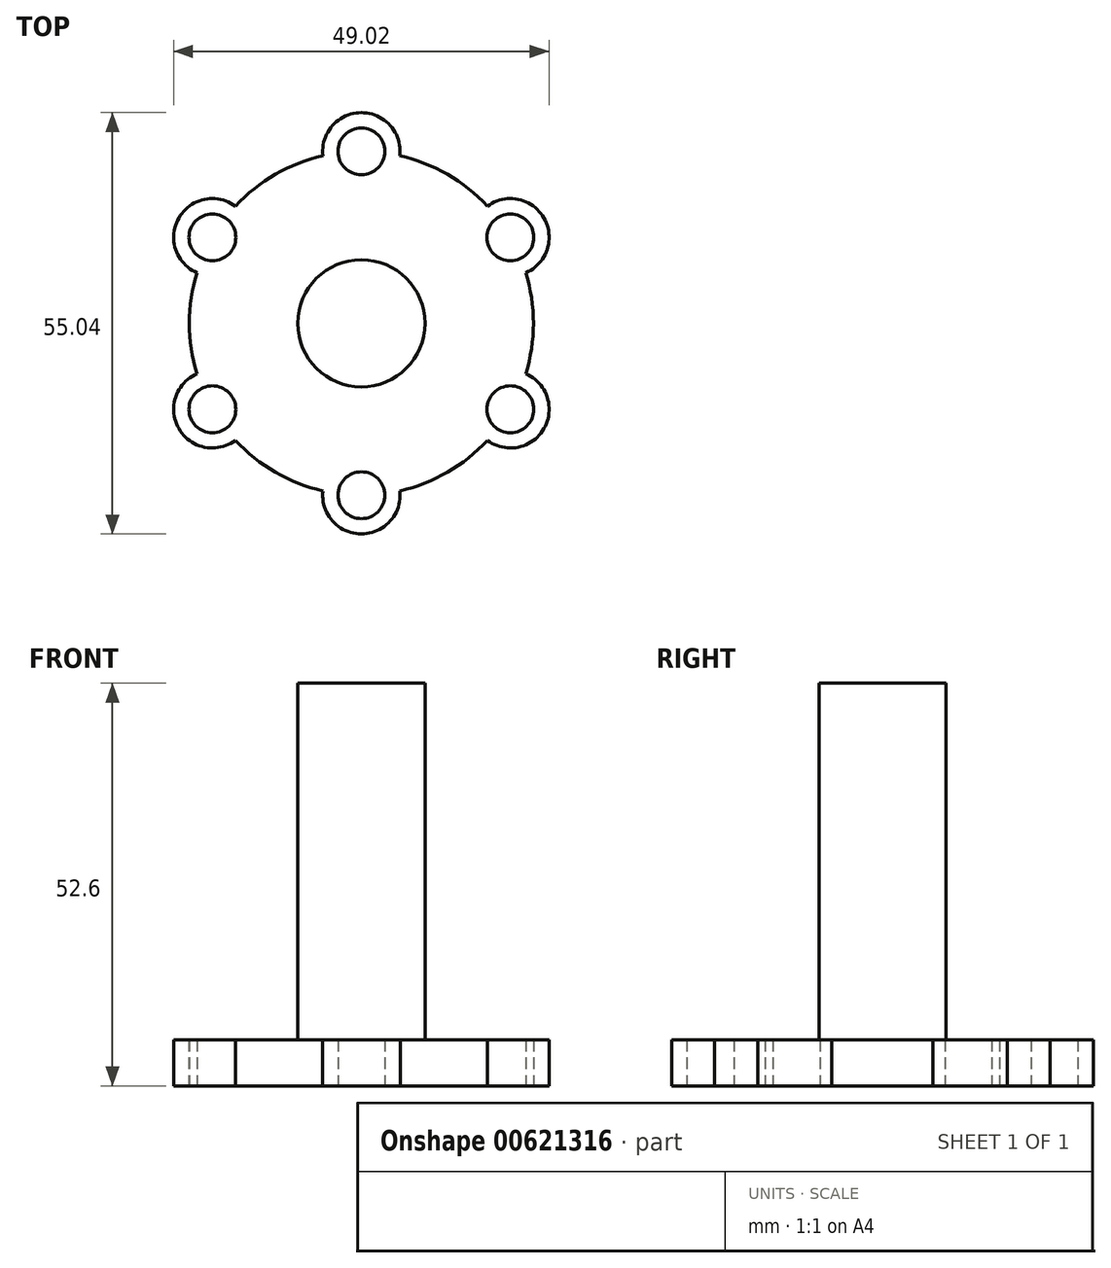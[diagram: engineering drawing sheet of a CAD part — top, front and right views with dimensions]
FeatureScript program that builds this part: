
annotation { "Feature Type Name" : "Feature", "Feature Type Description" : "" }
export const myFeature = defineFeature(function(context is Context, id is Id, definition is map)
    precondition{}
    {
        {
            var Q0;
            Q0=qCreatedBy(makeId("Top.planeOp"),FACE);
            var sketch = newSketch(context, id + "F0", { "sketchPlane" : qUnion([Q0])});
            skCircle(sketch, "E0", {"center": v(0, 0) * mm, "radius": 22.46 * mm});
            skCircle(sketch, "E1", {"center": v(0, 0) * mm, "radius": 8.3 * mm});
            skArc(sketch, "E2", {"start": v(3.05, 22.25) * mm, "mid": v(0, 25.52) * mm, "end": v(-3.05, 22.25) * mm});
            skCircle(sketch, "E3.0", {"center": v(0, 0) * mm, "radius": 20.46 * mm});
            skArc(sketch, "E4.0", {"start": v(5.03, 21.9) * mm, "mid": v(0, 27.52) * mm, "end": v(-5.03, 21.9) * mm});
            skArc(sketch, "E5.1.0", {"start": v(-16.45, 15.3) * mm, "mid": v(-23.83, 13.76) * mm, "end": v(-21.47, 6.6) * mm});
            skArc(sketch, "E5.1.1", {"start": v(-17.75, 13.77) * mm, "mid": v(-22.1, 12.76) * mm, "end": v(-20.8, 8.48) * mm});
            skArc(sketch, "E5.2.0", {"start": v(-21.47, -6.6) * mm, "mid": v(-23.83, -13.76) * mm, "end": v(-16.45, -15.3) * mm});
            skArc(sketch, "E5.2.1", {"start": v(-20.8, -8.48) * mm, "mid": v(-22.1, -12.76) * mm, "end": v(-17.75, -13.77) * mm});
            skArc(sketch, "E5.3.0", {"start": v(-5.03, -21.9) * mm, "mid": v(0, -27.52) * mm, "end": v(5.03, -21.9) * mm});
            skArc(sketch, "E5.3.1", {"start": v(-3.05, -22.25) * mm, "mid": v(0, -25.52) * mm, "end": v(3.05, -22.25) * mm});
            skArc(sketch, "E5.4.0", {"start": v(16.45, -15.3) * mm, "mid": v(23.83, -13.76) * mm, "end": v(21.47, -6.6) * mm});
            skArc(sketch, "E5.4.1", {"start": v(17.75, -13.77) * mm, "mid": v(22.1, -12.76) * mm, "end": v(20.8, -8.48) * mm});
            skArc(sketch, "E5.5.0", {"start": v(21.47, 6.6) * mm, "mid": v(23.83, 13.76) * mm, "end": v(16.45, 15.3) * mm});
            skArc(sketch, "E5.5.1", {"start": v(20.8, 8.48) * mm, "mid": v(22.1, 12.76) * mm, "end": v(17.75, 13.77) * mm});
            skCircle(sketch, "E6", {"center": v(-19.45, -11.23) * mm, "radius": 3.06 * mm});
            skCircle(sketch, "E7.1.1", {"center": v(0, -22.46) * mm, "radius": 3.06 * mm});
            skCircle(sketch, "E7.2.1", {"center": v(19.45, -11.23) * mm, "radius": 3.06 * mm});
            skCircle(sketch, "E7.3.1", {"center": v(19.45, 11.23) * mm, "radius": 3.06 * mm});
            skCircle(sketch, "E7.4.1", {"center": v(0, 22.46) * mm, "radius": 3.06 * mm});
            skCircle(sketch, "E7.5.1", {"center": v(-19.45, 11.23) * mm, "radius": 3.06 * mm});
            skSolve(sketch);
        }
        {
            var Q0;
            Q0=makeQuery(id+"F0.imprint","IMPRINT",FACE,{"disambiguationData":[TD([[makeQuery(id+"F0.imprint","IMPRINT",EDGE,{"derivedFrom":sQuery(id+"F0.wireOp",EDGE,"E1")}),1.0]])]});
            extrude(context, id + "F1", {"entities" : qUnion([Q0]), "depth" : 52.6 * mm, "offsetDistance" : 25 * mm});
        }
        {
            var Q0;
            {var subQ5=sQuery(id+"F0.wireOp",EDGE,"E0");var subQ8=makeQuery(id+"F0.imprint","INTERSECT",VERTEX,{"disambiguationData":[OD(1.0)],"derivedFrom":[subQ5,sQuery(id+"F0.wireOp",EDGE,"E5.5.0")]});Q0=makeQuery(id+"F0.imprint","IMPRINT",FACE,{"disambiguationData":[TD([[makeQuery(id+"F0.imprint","IMPRINT",EDGE,{"disambiguationData":[TD([[subQ8,1.0]])],"derivedFrom":subQ5}),1.0]])]});}
            var Q1;
            {var subQ0=sQuery(id+"F0.wireOp",EDGE,"E4.0");Q1=makeQuery(id+"F0.imprint","IMPRINT",FACE,{"disambiguationData":[TD([[makeQuery(id+"F0.imprint","IMPRINT",EDGE,{"derivedFrom":subQ0}),1.0]])]});}
            var Q2;
            {var subQ0=sQuery(id+"F0.wireOp",EDGE,"E5.5.0");Q2=makeQuery(id+"F0.imprint","IMPRINT",FACE,{"disambiguationData":[TD([[makeQuery(id+"F0.imprint","IMPRINT",EDGE,{"derivedFrom":subQ0}),1.0]])]});}
            var Q3;
            {var subQ5=sQuery(id+"F0.wireOp",EDGE,"E0");var subQ7=makeQuery(id+"F0.imprint","INTERSECT",VERTEX,{"disambiguationData":[OD(0.0)],"derivedFrom":[subQ5,sQuery(id+"F0.wireOp",EDGE,"E5.5.0")]});Q3=makeQuery(id+"F0.imprint","IMPRINT",FACE,{"disambiguationData":[TD([[makeQuery(id+"F0.imprint","IMPRINT",EDGE,{"disambiguationData":[TD([[subQ7,-1.0]])],"derivedFrom":subQ5}),1.0]])]});}
            var Q4;
            {var subQ0=sQuery(id+"F0.wireOp",EDGE,"E0");var subQ8=makeQuery(id+"F0.imprint","INTERSECT",VERTEX,{"disambiguationData":[OD(1.0)],"derivedFrom":[subQ0,sQuery(id+"F0.wireOp",EDGE,"E5.3.0")]});Q4=makeQuery(id+"F0.imprint","IMPRINT",FACE,{"disambiguationData":[TD([[makeQuery(id+"F0.imprint","IMPRINT",EDGE,{"disambiguationData":[TD([[subQ8,1.0]])],"derivedFrom":subQ0}),1.0]])]});}
            var Q5;
            {var subQ0=sQuery(id+"F0.wireOp",EDGE,"E5.4.0");Q5=makeQuery(id+"F0.imprint","IMPRINT",FACE,{"disambiguationData":[TD([[makeQuery(id+"F0.imprint","IMPRINT",EDGE,{"derivedFrom":subQ0}),1.0]])]});}
            var Q6;
            {var subQ0=sQuery(id+"F0.wireOp",EDGE,"E5.3.0");Q6=makeQuery(id+"F0.imprint","IMPRINT",FACE,{"disambiguationData":[TD([[makeQuery(id+"F0.imprint","IMPRINT",EDGE,{"derivedFrom":subQ0}),1.0]])]});}
            var Q7;
            {var subQ5=sQuery(id+"F0.wireOp",EDGE,"E0");var subQ8=makeQuery(id+"F0.imprint","INTERSECT",VERTEX,{"disambiguationData":[OD(1.0)],"derivedFrom":[subQ5,sQuery(id+"F0.wireOp",EDGE,"E5.2.0")]});Q7=makeQuery(id+"F0.imprint","IMPRINT",FACE,{"disambiguationData":[TD([[makeQuery(id+"F0.imprint","IMPRINT",EDGE,{"disambiguationData":[TD([[subQ8,1.0]])],"derivedFrom":subQ5}),1.0]])]});}
            var Q8;
            {var subQ0=sQuery(id+"F0.wireOp",EDGE,"E0");var subQ4=makeQuery(id+"F0.imprint","INTERSECT",VERTEX,{"disambiguationData":[OD(1.0)],"derivedFrom":[subQ0,sQuery(id+"F0.wireOp",EDGE,"E5.1.0")]});Q8=makeQuery(id+"F0.imprint","IMPRINT",FACE,{"disambiguationData":[TD([[makeQuery(id+"F0.imprint","IMPRINT",EDGE,{"disambiguationData":[TD([[subQ4,1.0]])],"derivedFrom":subQ0}),1.0]])]});}
            var Q9;
            {var subQ5=sQuery(id+"F0.wireOp",EDGE,"E0");var subQ6=makeQuery(id+"F0.imprint","INTERSECT",VERTEX,{"disambiguationData":[OD(1.0)],"derivedFrom":[subQ5,sQuery(id+"F0.wireOp",EDGE,"E4.0")]});Q9=makeQuery(id+"F0.imprint","IMPRINT",FACE,{"disambiguationData":[TD([[makeQuery(id+"F0.imprint","IMPRINT",EDGE,{"disambiguationData":[TD([[subQ6,1.0]])],"derivedFrom":subQ5}),1.0]])]});}
            var Q10;
            {var subQ0=sQuery(id+"F0.wireOp",EDGE,"E5.1.0");Q10=makeQuery(id+"F0.imprint","IMPRINT",FACE,{"disambiguationData":[TD([[makeQuery(id+"F0.imprint","IMPRINT",EDGE,{"derivedFrom":subQ0}),1.0]])]});}
            var Q11;
            {var subQ0=sQuery(id+"F0.wireOp",EDGE,"E5.2.0");Q11=makeQuery(id+"F0.imprint","IMPRINT",FACE,{"disambiguationData":[TD([[makeQuery(id+"F0.imprint","IMPRINT",EDGE,{"derivedFrom":subQ0}),1.0]])]});}
            var Q12;
            Q12=makeQuery(id+"F0.imprint","IMPRINT",FACE,{"disambiguationData":[TD([[makeQuery(id+"F0.imprint","IMPRINT",EDGE,{"derivedFrom":sQuery(id+"F0.wireOp",EDGE,"E1")}),-1.0]])]});
            extrude(context, id + "F2", {"entities" : qUnion([Q0, Q1, Q2, Q3, Q4, Q5, Q6, Q7, Q8, Q9, Q10, Q11, Q12]), "operationType" : NewBodyOperationType.ADD, "depth" : 6 * mm, "offsetDistance" : 25 * mm});
        }
    });
